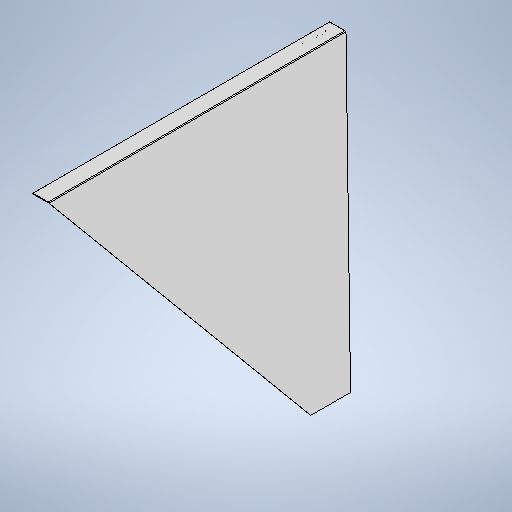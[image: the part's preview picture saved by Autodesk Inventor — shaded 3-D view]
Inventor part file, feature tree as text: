
AUTODESK INVENTOR PART (.ipt)
format: ipt  version: 2025 (Build 290162010, 162A)  size: 419,328 bytes
history: native  units: mm
features: other x7, sheet_metal_op x3, sketch x3, reference x2, extrude x1
ambient origin geometry x8: Origin, YZ Plane, XZ Plane, XY Plane, X Axis, Y Axis, Z Axis, Center Point
bodies: Body1 (feature_tree)
feature tree (16):
  sheet_metal_op  "Contour Flange2"
  extrude  "Extrusion13"  Depth=100.0mm
  other  "Mark2"
  other  "A-Side Definition"
  sketch  "Sketch1"  dims[d0=1150.0mm d61=100.0mm]
  other  "Plate4"
  sheet_metal_op  "Bend4"
  sheet_metal_op  "Corner4"
  sketch  "Sketch17"  dims[d66=6.0mm]
  reference  "Reference1"
  reference  "Reference2"
  sketch  "Sketch19"  dims[d68=230.0mm d69=4.0mm d70=4.0mm d71=2.0mm d72=8.0mm d73=6.0mm d74=1500.0mm d75=6.0mm d76=4.0mm d77=16.0mm d78=4.0mm d79=6.0mm d83=855.0mm d87=20.666414mm d90=80.0mm d111=0.0mm d112=0.0mm d113=6.0mm]
  other  "ASY MSC 100 cone.iam"
  other  "MSC 114 cone IN right board.ipt:1"
  other  "MSC 113 cone IN left board.ipt:1"
  other  "Definition1"
